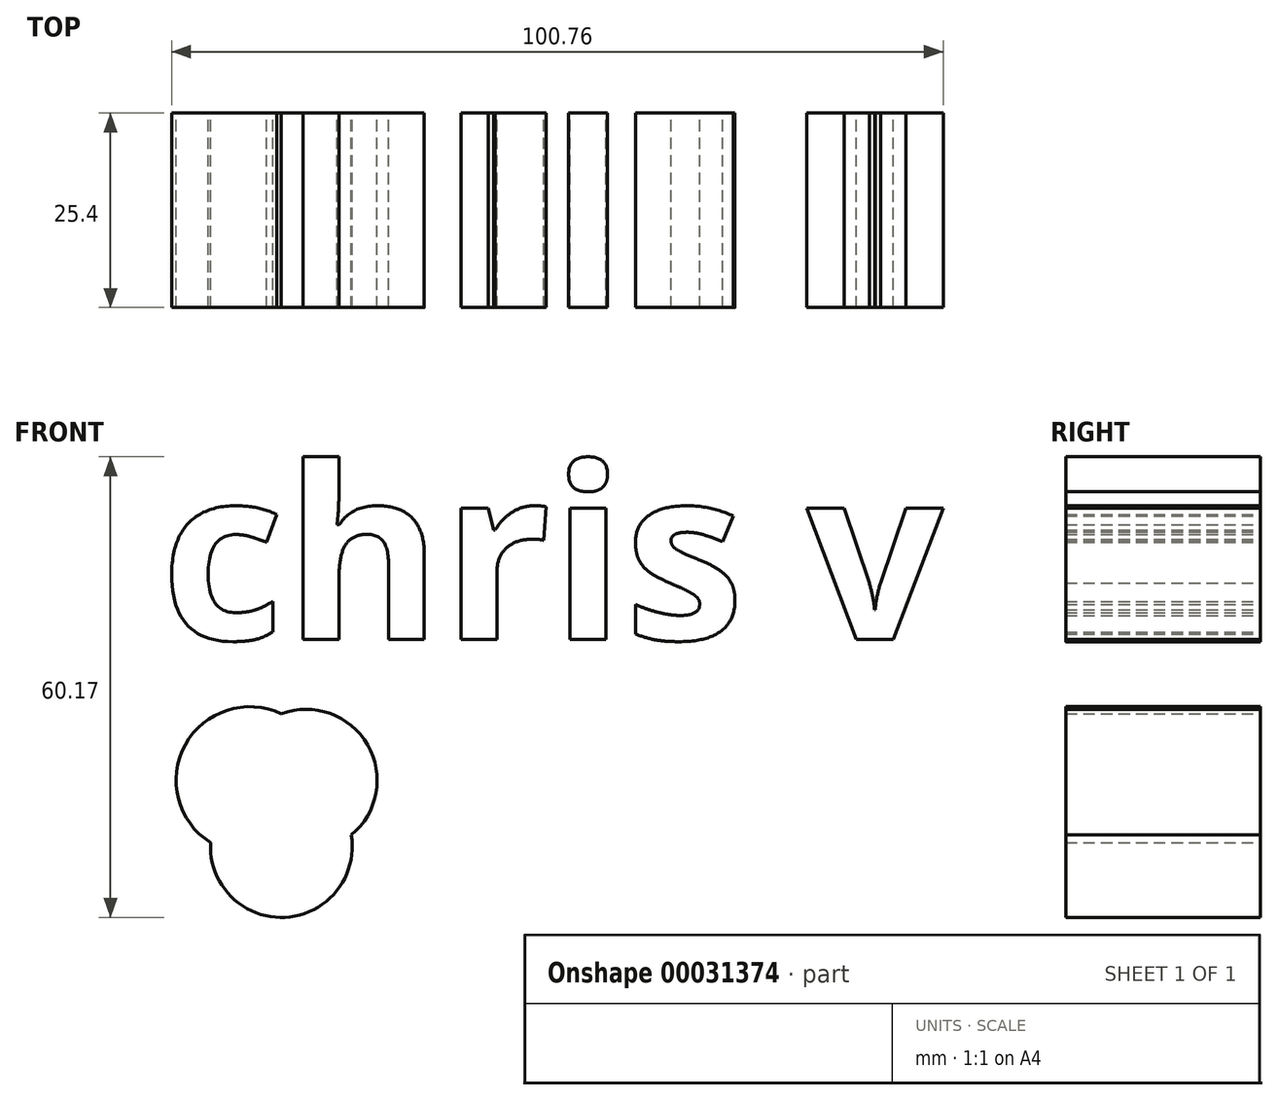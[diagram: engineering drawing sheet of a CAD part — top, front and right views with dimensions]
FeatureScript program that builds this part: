
annotation { "Feature Type Name" : "Feature", "Feature Type Description" : "" }
export const myFeature = defineFeature(function(context is Context, id is Id, definition is map)
    precondition{}
    {
        {
            var Q0;
            Q0=qCreatedBy(makeId("Front.planeOp"),FACE);
            var sketch = newSketch(context, id + "F0", { "sketchPlane" : qUnion([Q0])});
            skText(sketch, "E0", { "text": "chris v", "fontName": "OpenSans-Bold.ttf"});
            const initialGuessF0  = {"E0": [-0.04689, -0.00636, 1, 0, 0.02259]};
            skSetInitialGuess(sketch, initialGuessF0);
            skSolve(sketch);
        }
        {
            var Q0;
            Q0 = qSketchRegion(id + "F0", true);
            extrude(context, id + "F1", {"entities" : qUnion([Q0]), "depth" : 25.4 * mm});
        }
        {
            var Q0;
            Q0=qCreatedBy(makeId("Front.planeOp"),FACE);
            var sketch = newSketch(context, id + "F2", { "sketchPlane" : qUnion([Q0])});
            skCircle(sketch, "E1", {"center": v(-35.3, -24.77) * mm, "radius": 9.6 * mm});
            skCircle(sketch, "E2", {"center": v(-27.9, -24.77) * mm, "radius": 9.26 * mm});
            skCircle(sketch, "E3", {"center": v(-31.16, -33.44) * mm, "radius": 9.26 * mm});
            skSolve(sketch);
        }
        {
            var Q0;
            {var subQ0=sQuery(id+"F2.wireOp",EDGE,"E3");var subQ3=sQuery(id+"F2.wireOp",EDGE,"E1");var subQ4=makeQuery(id+"F2.imprint","INTERSECT",VERTEX,{"disambiguationData":[OD(0.0)],"derivedFrom":[subQ3,subQ0]});Q0=makeQuery(id+"F2.imprint","IMPRINT",FACE,{"disambiguationData":[TD([[makeQuery(id+"F2.imprint","IMPRINT",EDGE,{"disambiguationData":[TD([[subQ4,1.0]])],"derivedFrom":subQ3}),1.0]])]});}
            var Q1;
            {var subQ1=sQuery(id+"F2.wireOp",EDGE,"E2");var subQ3=sQuery(id+"F2.wireOp",EDGE,"E1");var subQ5=makeQuery(id+"F2.imprint","INTERSECT",VERTEX,{"disambiguationData":[OD(0.0)],"derivedFrom":[subQ3,subQ1]});Q1=makeQuery(id+"F2.imprint","IMPRINT",FACE,{"disambiguationData":[TD([[makeQuery(id+"F2.imprint","IMPRINT",EDGE,{"disambiguationData":[TD([[subQ5,1.0]])],"derivedFrom":subQ3}),1.0]])]});}
            var Q2;
            {var subQ1=sQuery(id+"F2.wireOp",EDGE,"E1");var subQ3=sQuery(id+"F2.wireOp",EDGE,"E2");var subQ5=makeQuery(id+"F2.imprint","INTERSECT",VERTEX,{"disambiguationData":[OD(0.0)],"derivedFrom":[subQ1,subQ3]});Q2=makeQuery(id+"F2.imprint","IMPRINT",FACE,{"disambiguationData":[TD([[makeQuery(id+"F2.imprint","IMPRINT",EDGE,{"disambiguationData":[TD([[subQ5,1.0]])],"derivedFrom":subQ1}),-1.0]])]});}
            var Q3;
            {var subQ1=sQuery(id+"F2.wireOp",EDGE,"E2");var subQ3=sQuery(id+"F2.wireOp",EDGE,"E1");var subQ5=makeQuery(id+"F2.imprint","INTERSECT",VERTEX,{"disambiguationData":[OD(1.0)],"derivedFrom":[subQ3,subQ1]});Q3=makeQuery(id+"F2.imprint","IMPRINT",FACE,{"disambiguationData":[TD([[makeQuery(id+"F2.imprint","IMPRINT",EDGE,{"disambiguationData":[TD([[subQ5,-1.0]])],"derivedFrom":subQ3}),1.0]])]});}
            var Q4;
            {var subQ0=sQuery(id+"F2.wireOp",EDGE,"E3");var subQ3=sQuery(id+"F2.wireOp",EDGE,"E1");var subQ4=makeQuery(id+"F2.imprint","INTERSECT",VERTEX,{"disambiguationData":[OD(0.0)],"derivedFrom":[subQ3,subQ0]});Q4=makeQuery(id+"F2.imprint","IMPRINT",FACE,{"disambiguationData":[TD([[makeQuery(id+"F2.imprint","IMPRINT",EDGE,{"disambiguationData":[TD([[subQ4,-1.0]])],"derivedFrom":subQ3}),1.0]])]});}
            var Q5;
            {var subQ1=sQuery(id+"F2.wireOp",EDGE,"E1");var subQ3=sQuery(id+"F2.wireOp",EDGE,"E2");var subQ5=makeQuery(id+"F2.imprint","INTERSECT",VERTEX,{"disambiguationData":[OD(1.0)],"derivedFrom":[subQ1,subQ3]});Q5=makeQuery(id+"F2.imprint","IMPRINT",FACE,{"disambiguationData":[TD([[makeQuery(id+"F2.imprint","IMPRINT",EDGE,{"disambiguationData":[TD([[subQ5,-1.0]])],"derivedFrom":subQ1}),-1.0]])]});}
            var Q6;
            {var subQ0=sQuery(id+"F2.wireOp",EDGE,"E3");var subQ3=sQuery(id+"F2.wireOp",EDGE,"E1");var subQ4=makeQuery(id+"F2.imprint","INTERSECT",VERTEX,{"disambiguationData":[OD(0.0)],"derivedFrom":[subQ3,subQ0]});Q6=makeQuery(id+"F2.imprint","IMPRINT",FACE,{"disambiguationData":[TD([[makeQuery(id+"F2.imprint","IMPRINT",EDGE,{"disambiguationData":[TD([[subQ4,-1.0]])],"derivedFrom":subQ3}),-1.0]])]});}
            extrude(context, id + "F3", {"entities" : qUnion([Q0, Q1, Q2, Q3, Q4, Q5, Q6]), "depth" : 25.4 * mm});
        }
    });
